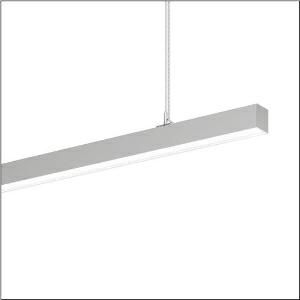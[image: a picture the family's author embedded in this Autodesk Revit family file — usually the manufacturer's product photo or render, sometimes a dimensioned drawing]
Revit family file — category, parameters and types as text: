
# Revit family: silica_r__21_51mx33db49sb_c15f
name_source: partatom
category: Lighting Fixtures
units: mm (PartAtom-declared; Revit-internal decimal feet)

## family parameters
Cut with Voids When Loaded = No
Host = Face
Light Source = No
Part Type = Normal
Room Calculation Point = No
Round Connector Dimension = Use Diameter
Shared = No

## types (1)
- --- (1 x LED, 7390 lm, 48.3 W, 4000K)
    Apparent Load = 48 VA
    CIE Flux Codes = 78 96 99 55 100
    Color Rendering = 80
    Color Temperature = 4000K
    Default Elevation = 1800 mm
    Description = Silica® 21, office luminaire, primary optical cover: prismatic diffuser, of PMMA, CAT 2 (L<= 3000cd/m²), light emission: direct/indirect distribution, primary light characteristic: symmetric, installation type: suspended mounting, LED, rated luminous flux: 7.390lm, luminous efficacy: 153lm/W, light colour: 840, colour temperature: 4000K, with terminal, 3+2-pole, max. 2.5mm², mains connection: 220..240V, AC, 50/60Hz, rated input power: 48.3W, luminaire housing, of aluminium, metallic grey (RAL 9006), length: 1.504mm, width: 53mm, height: 53mm, protection rating (complete): IP20, insulation class (complete): insulation class I (protective earthing), certification: CE, permissible operating ambient temperature: 0..+35°C, standard: EN 50419, packaging unit: 1 piece
    Height = 53 mm
    Lamp = 1 x LED
    Lamp Light Flux = 7390 lm
    Lamp Power = 48.3 W
    Lamp count = 1
    Length = 1504 mm
    Luminous efficacy = 153 lm/W
    Manufacturer = Siteco
    ModVariant = No
    Model = 51MX33DB49SB
    Mounting Place = Ceiling
    Mounting Type = Pendant
    Number of Poles = 1
    OnlyDefault = Yes
    Power Factor = 1
    Product Name = Silica® 21
    Product group = office luminaire | ceiling pendant
    ProductGroupID = 902
    Protection Class = Protection class I
    Protection Degree = IP 20
    RLX_Detail_Level = 1
    RLX_Emergency_Light_Flux = 0 lm
    RLX_Emergency_Type = 0
    RLX_Emergency_Type_DB = No
    RlxData = <blob elided: 23545 chars, md5=82a26d92>
    Socket = socket
    Standby Power = 0 W
    System Light Flux = 7390 lm
    System Power = 48 W
    Type Comments = factory setting: luminous flux: 100 % | dim-lin: 254 | 323 mA
    Type Image = l_1313621.jpg
    URL = http://relux.com
    VarID = @adj_066853
    Voltage = 0 V
    Weight = 0.00 kg
    Width = 53 mm

## geometry (parser evidence)
native form markers: Blend x4, Sweep x13
no freeform markers — native parametric forms only
